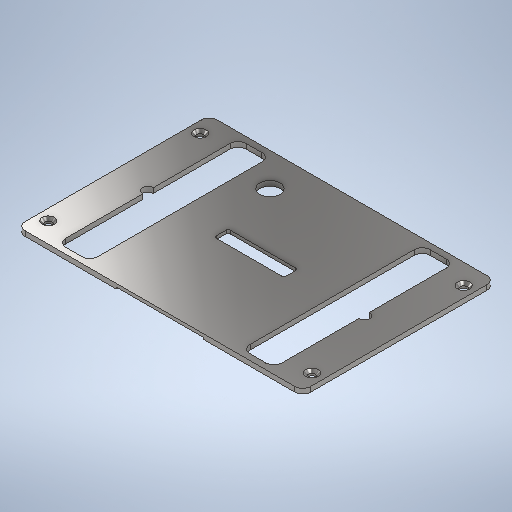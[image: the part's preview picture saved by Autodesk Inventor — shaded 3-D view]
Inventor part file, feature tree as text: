
AUTODESK INVENTOR PART (.ipt)
format: ipt  version: 2025 (Build 290162000, 162)  size: 384,512 bytes
history: native  units: in
note: dims shown in document units (in); Inventor stores cm internally (conversion verified against a paired STEP export)
features: extrude x6, sketch x5, hole x1, fillet x1
ambient origin geometry x8: Origin, YZ Plane, XZ Plane, XY Plane, X Axis, Y Axis, Z Axis, Center Point
bodies: Solid1 (feature_tree)
feature tree (13):
  extrude  "Extrusion1"  Depth=2.815in
  hole  "Hole1"  [1 undecoded]
  fillet  "Fillet3"  Radius=0.748in
  extrude  "Extrusion7"  Depth=0.0787in
  extrude  "Extrusion8"  Depth=0.0591in
  extrude  "Extrusion9"  Depth=0.315in
  extrude  "Extrusion10"  Depth=0.315in
  extrude  "Extrusion11"  TaperAngle=0.0deg  [1 undecoded]
  sketch  "Sketch10"  dims[d0=1.8937in d1=2.815in]
  sketch  "Sketch11"  dims[d3=0.0484in d4=0.0in]
  sketch  "Sketch12"  dims[d9=0.07in d10=0.146in d11=0.119in d12=0.25in d13=0.5635in d14=1.0in d15=0.8108in d77=1.4961in d78=0.748in]
  sketch  "Sketch13"  dims[d79=1.2992in d114=0.0787in]
  sketch  "Sketch15"  dims[d115=1.2992in d124=0.0591in d125=1.6535in d126=1.0846in d127=0.0in d128=0.0in d129=0.8661in d130=1.1811in d131=0.4331in d132=0.0787in d133=0.0169in d134=0.0in d135=0.689in d136=0.1378in d137=0.0197in d138=0.0in d139=0.0in d146=0.0in d147=0.0in d161=0.6201in d162=0.4823in d163=0.1969in d164=1.7756in d165=1.065in d166=0.0787in d167=0.315in d168=0.0in d169=0.0in d170=1.0689in d171=0.1024in]
note: 2 required parameter values undecoded (feature->parameter linkage not recoverable at this tier; creation-order binding heuristic only, values carry confidence <= 0.55)
